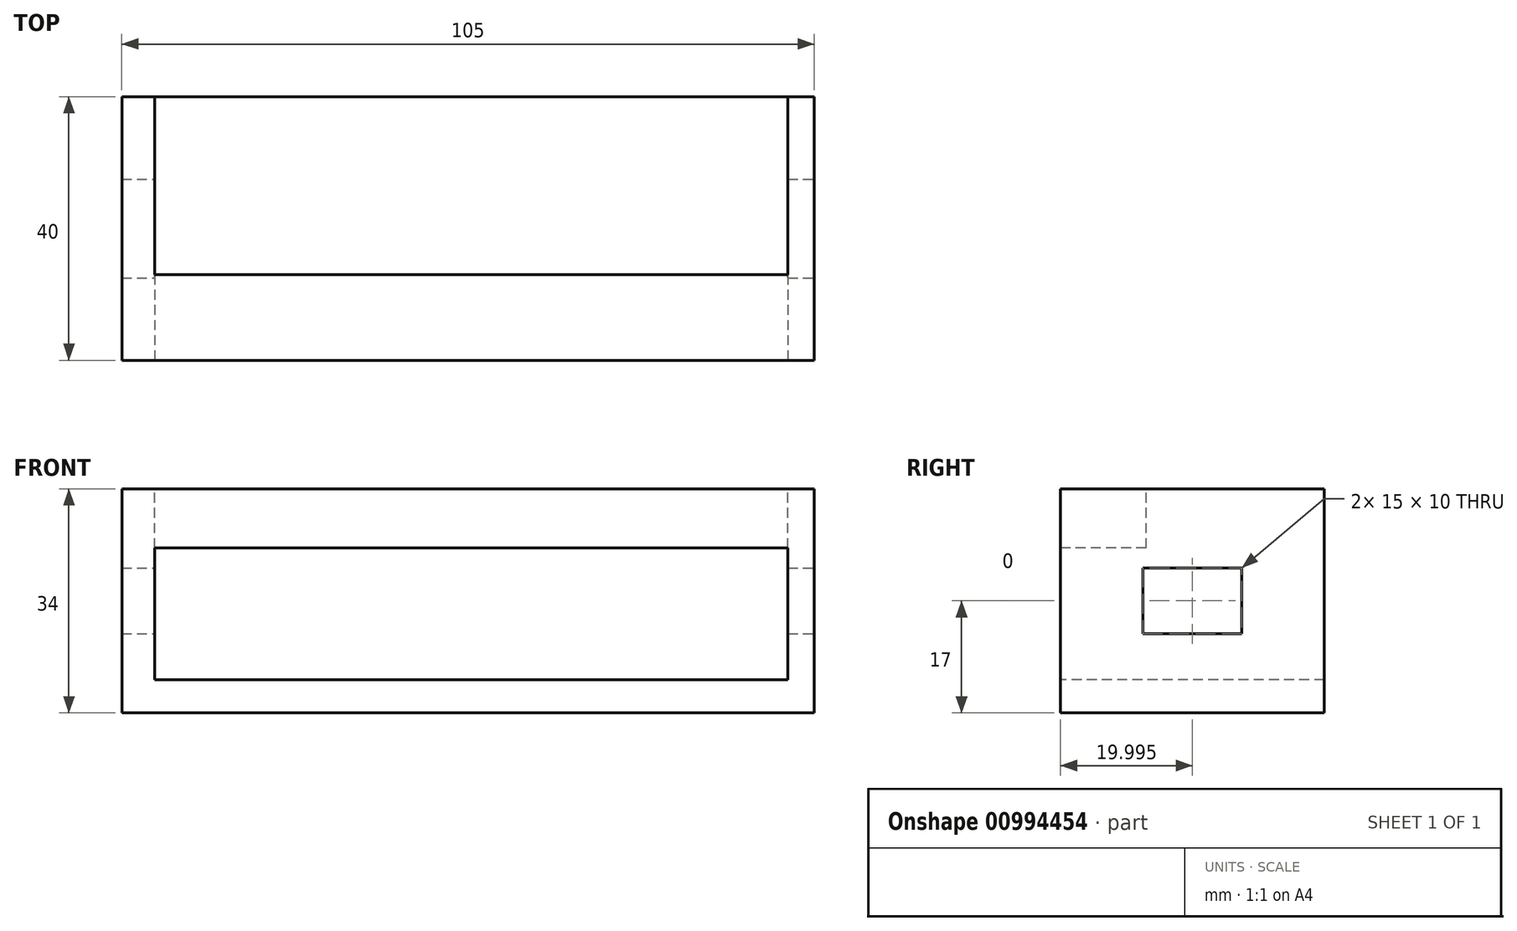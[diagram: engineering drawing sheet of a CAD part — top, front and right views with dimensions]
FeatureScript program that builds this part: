
annotation { "Feature Type Name" : "Feature", "Feature Type Description" : "" }
export const myFeature = defineFeature(function(context is Context, id is Id, definition is map)
    precondition{}
    {
        {
            var Q0;
            Q0=qCreatedBy(makeId("Top.planeOp"),FACE);
            var sketch = newSketch(context, id + "F0", { "sketchPlane" : qUnion([Q0])});
            skLineSegment(sketch, "E0.bottom", {"start": v(-44.1, -37.62) * mm, "end": v(60.9, -37.62) * mm});
            skLineSegment(sketch, "E0.top", {"start": v(-44.1, 2.38) * mm, "end": v(60.9, 2.38) * mm});
            skLineSegment(sketch, "E0.left", {"start": v(-44.1, -37.62) * mm, "end": v(-44.1, 2.38) * mm});
            skLineSegment(sketch, "E0.right", {"start": v(60.9, -37.62) * mm, "end": v(60.9, 2.38) * mm});
            skSolve(sketch);
        }
        {
            var Q0;
            Q0=makeQuery(id+"F0.imprint","IMPRINT",FACE,{"disambiguationData":[TD([[makeQuery(id+"F0.imprint","IMPRINT",EDGE,{"derivedFrom":sQuery(id+"F0.wireOp",EDGE,"E0.bottom")}),1.0]])]});
            extrude(context, id + "F1", {"entities" : qUnion([Q0]), "depth" : 34 * mm, "offsetDistance" : 25 * mm});
        }
        {
            var Q0;
            Q0=makeQuery(id+"F1.opExtrude","SWEPT_FACE",FACE,{"disambiguationData":[OSD([sQuery(id+"F0.wireOp",EDGE,"E0.bottom")])]});
            var sketch = newSketch(context, id + "F2", { "sketchPlane" : qUnion([Q0])});
            skLineSegment(sketch, "E1.bottom", {"start": v(-39.1, 5) * mm, "end": v(56.9, 5) * mm});
            skLineSegment(sketch, "E1.top", {"start": v(-39.1, 25) * mm, "end": v(56.9, 25) * mm});
            skLineSegment(sketch, "E1.left", {"start": v(-39.1, 5) * mm, "end": v(-39.1, 25) * mm});
            skLineSegment(sketch, "E1.right", {"start": v(56.9, 5) * mm, "end": v(56.9, 25) * mm});
            skSolve(sketch);
        }
        {
            var Q0;
            Q0=makeQuery(id+"F2.imprint","IMPRINT",FACE,{"disambiguationData":[TD([[makeQuery(id+"F2.imprint","IMPRINT",EDGE,{"derivedFrom":sQuery(id+"F2.wireOp",EDGE,"E1.bottom")}),1.0]])]});
            extrude(context, id + "F3", {"entities" : qUnion([Q0]), "operationType" : NewBodyOperationType.REMOVE, "endBound" : BoundingType.THROUGH_ALL, "oppositeDirection" : true, "depth" : 25 * mm, "offsetDistance" : 25 * mm});
        }
        {
            var Q0;
            Q0=makeQuery(id+"F1.opExtrude","CAP_FACE",FACE,{"disambiguationData":[OSD([sQuery(id+"F0.wireOp",EDGE,"E0.bottom"),sQuery(id+"F0.wireOp",EDGE,"E0.top"),sQuery(id+"F0.wireOp",EDGE,"E0.left"),sQuery(id+"F0.wireOp",EDGE,"E0.right")])],"isStart":false});
            var sketch = newSketch(context, id + "F4", { "sketchPlane" : qUnion([Q0])});
            skLineSegment(sketch, "E2.bottom", {"start": v(-39.1, -24.62) * mm, "end": v(56.9, -24.62) * mm});
            skLineSegment(sketch, "E2.top", {"start": v(-39.1, 76.7) * mm, "end": v(56.9, 76.7) * mm});
            skLineSegment(sketch, "E2.left", {"start": v(-39.1, -24.62) * mm, "end": v(-39.1, 76.7) * mm});
            skLineSegment(sketch, "E2.right", {"start": v(56.9, -24.62) * mm, "end": v(56.9, 76.7) * mm});
            skSolve(sketch);
        }
        {
            var Q0;
            {var subQ0=sQuery(id+"F4.wireOp",EDGE,"E2.bottom");Q0=makeQuery(id+"F4.imprint","IMPRINT",FACE,{"disambiguationData":[TD([[makeQuery(id+"F4.imprint","IMPRINT",EDGE,{"derivedFrom":subQ0}),1.0]])]});}
            extrude(context, id + "F5", {"entities" : qUnion([Q0]), "operationType" : NewBodyOperationType.REMOVE, "oppositeDirection" : true, "depth" : 10 * mm, "offsetDistance" : 25 * mm});
        }
        {
            var Q0;
            Q0=makeQuery(id+"F1.opExtrude","SWEPT_FACE",FACE,{"disambiguationData":[OSD([sQuery(id+"F0.wireOp",EDGE,"E0.right")])]});
            var sketch = newSketch(context, id + "F6", { "sketchPlane" : qUnion([Q0])});
            skLineSegment(sketch, "E3.bottom", {"start": v(-25.12, 12) * mm, "end": v(-10.12, 12) * mm});
            skLineSegment(sketch, "E3.top", {"start": v(-25.12, 22) * mm, "end": v(-10.12, 22) * mm});
            skLineSegment(sketch, "E3.left", {"start": v(-25.12, 12) * mm, "end": v(-25.12, 22) * mm});
            skLineSegment(sketch, "E3.right", {"start": v(-10.12, 12) * mm, "end": v(-10.12, 22) * mm});
            skSolve(sketch);
        }
        {
            var Q0;
            Q0=makeQuery(id+"F6.imprint","IMPRINT",FACE,{"disambiguationData":[TD([[makeQuery(id+"F6.imprint","IMPRINT",EDGE,{"derivedFrom":sQuery(id+"F6.wireOp",EDGE,"E3.bottom")}),1.0]])]});
            extrude(context, id + "F7", {"entities" : qUnion([Q0]), "operationType" : NewBodyOperationType.REMOVE, "endBound" : BoundingType.THROUGH_ALL, "oppositeDirection" : true, "depth" : 25 * mm, "offsetDistance" : 25 * mm});
        }
    });
